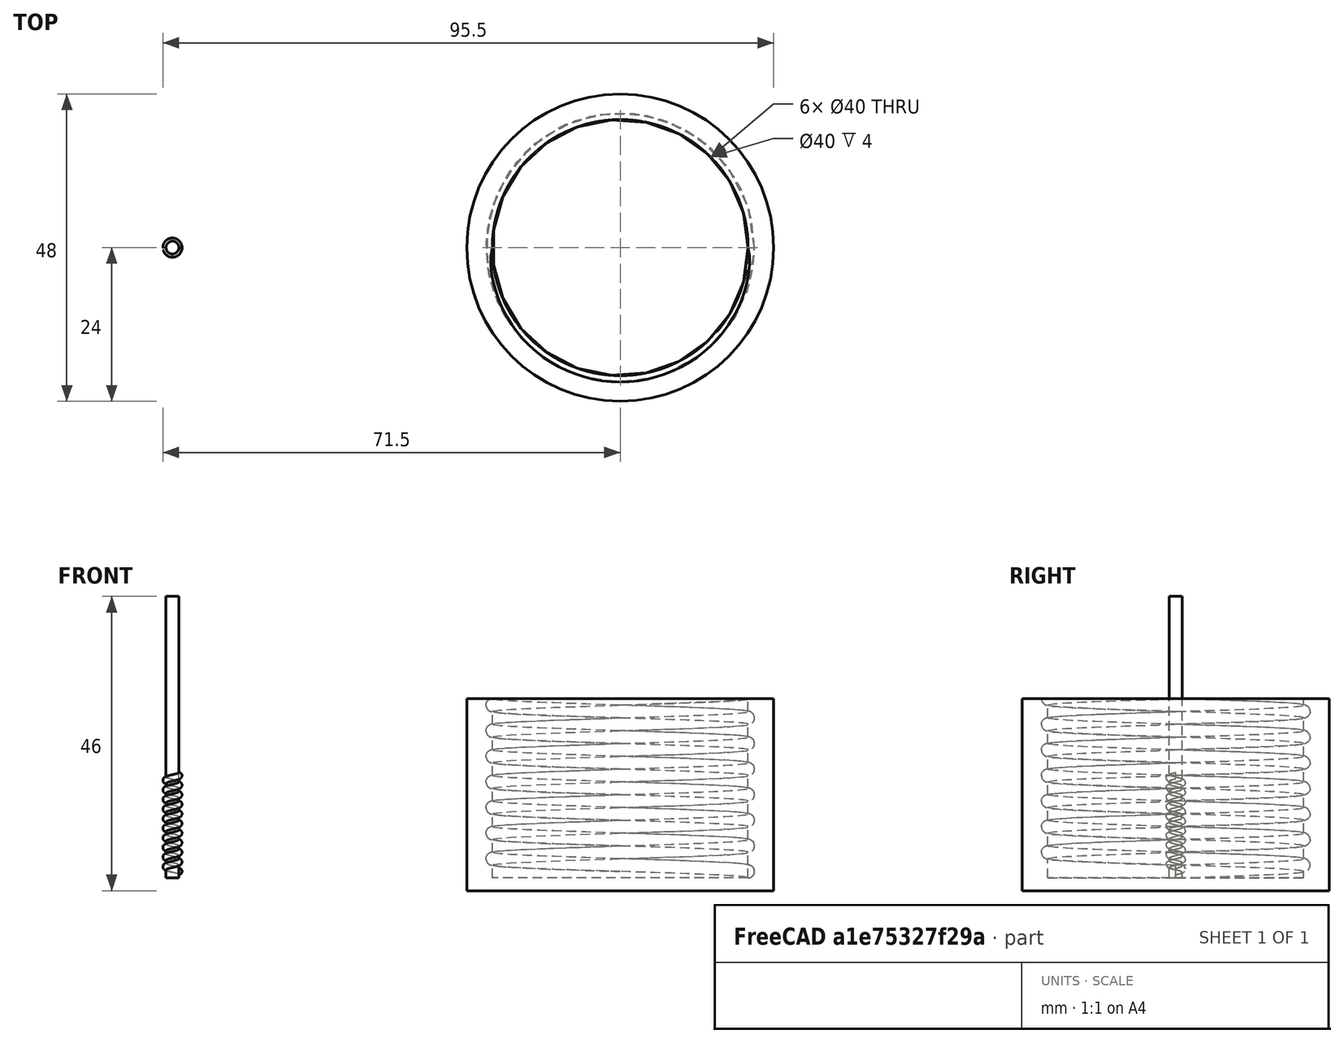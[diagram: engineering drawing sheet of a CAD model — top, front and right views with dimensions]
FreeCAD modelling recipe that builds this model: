
FCSTD DOCUMENT  (FreeCAD 0.19R)
Label: roscas
License: Creative Commons Attribution-ShareAlike
LicenseURL: http://creativecommons.org/licenses/by-sa/4.0/
objects: Part::Cylinder×3, App::DocumentObjectGroup×3, Part::Helix×2, Sketcher::SketchObject×2, Part::Sweep×2, Part::Fuse×2, PartDesign::Body×1, Part::Cut×1, Part::Feature×1, Mesh::Feature×1
note: 14 computed .brp shape members not serialized (recipe doc carries the construction recipe); baked Part::Feature solids carry a one-line shape summary decoded from their .brp

FEATURE [Part::Helix] Helix  label="Hélice"
  Angle = 0
  AttacherType = Attacher::AttachEngine3D
  Height = 40
  LocalCoord = 0
  Pitch = 4
  Radius = 20
  Style = 1
FEATURE [Sketcher::SketchObject] Sketch
  FullyConstrained = true
  MapMode = 5
  Placement = pos=(0,0,0) rot=(1,0,0;1.5708rad)
  Support = -> [XZ_Plane]
  sketch-geometry (1):
    g0: Circle CenterX=20 CenterY=0 CenterZ=0 NormalX=0 NormalY=0 NormalZ=1 AngleXU=0 Radius=1
  constraints (3):
    c: PointOnObject(g0,g-1)
    c: Radius(g0) = 1
    c: DistanceX(g-1,g0) = 20
FEATURE [PartDesign::Body] Body
  Group = -> [Sketch]
  Origin = -> Origin
  Placement = pos=(26,0,0) rot=(0,0,1;0rad)
FEATURE [Part::Sweep] Sweep
  Frenet = true
  Sections = -> [Sketch]
  Solid = true
  Spine = -> Helix [Edge10,Edge9,Edge8,Edge7,Edge6,Edge5,Edge4,Edge3,Edge2,Edge1]
  Transition = 1
FEATURE [Part::Cylinder] Cylinder  label="Cilindro"
  Angle = 360
  AttacherType = Attacher::AttachEngine3D
  Height = 44
  Placement = pos=(0,0,-1) rot=(0,0,1;0rad)
  Radius = 20
FEATURE [Part::Fuse] Fusion  label="Rosca macho"
  Base = -> Sweep
  Placement = pos=(0,0,3) rot=(0,0,1;0rad)
  Refine = true
  Tool = -> Cylinder
FEATURE [Part::Cylinder] Cylinder001  label="Cilindro001"
  Angle = 360
  AttacherType = Attacher::AttachEngine3D
  Height = 30
  Radius = 24
FEATURE [Part::Cut] Cut
  Base = -> Cylinder001
  Placement = pos=(70,0,0) rot=(0,0,1;0rad)
  Refine = true
  Tool = -> Fusion
FEATURE [Sketcher::SketchObject] Sketch001
  FullyConstrained = true
  MapMode = 5
  Placement = pos=(0,0,0) rot=(1,0,0;1.5708rad)
  sketch-geometry (1):
    g0: Circle CenterX=1 CenterY=0 CenterZ=0 NormalX=0 NormalY=0 NormalZ=1 AngleXU=0 Radius=0.5
  constraints (3):
    c: PointOnObject(g0,g-1)
    c: Radius(g0) = 0.5
    c: DistanceX(g-1,g0) = 1
FEATURE [Part::Cylinder] Cylinder002  label="Cilindro002"
  Angle = 360
  AttacherType = Attacher::AttachEngine3D
  Height = 44
  Placement = pos=(0,0,-1) rot=(0,0,1;0rad)
  Radius = 1
FEATURE [Part::Helix] Helix001  label="Hélice001"
  Angle = 0
  AttacherType = Attacher::AttachEngine3D
  Height = 40
  LocalCoord = 0
  Pitch = 1.5
  Radius = 1
  Style = 1
FEATURE [Part::Sweep] Sweep001
  Frenet = true
  Sections = -> [Sketch001]
  Solid = true
  Spine = -> Helix001 [Edge10,Edge9,Edge8,Edge7,Edge6,Edge5,Edge4,Edge3,Edge2,Edge1]
  Transition = 1
FEATURE [Part::Fuse] Fusion001  label="Rosca macho001"
  Base = -> Sweep001
  Placement = pos=(0,0,3) rot=(0,0,1;0rad)
  Refine = true
  Tool = -> Cylinder002
FEATURE [Part::Feature] Fusion001001  label="Rosca macho002"
  Placement = pos=(0,0,3) rot=(0,0,1;0rad)
  shape: bbox 3.919 x 4.387 x 44 mm, 35 faces (baked)
FEATURE [App::DocumentObjectGroup] Grupo  label="Tutorial"
  Group = -> [Cut,Body]
FEATURE [App::DocumentObjectGroup] Grupo001  label="Original"
  Group = -> [Fusion001001,Fusion001]
FEATURE [App::DocumentObjectGroup] Grupo002
FEATURE [Mesh::Feature] Ex04_15x50plus30x4
